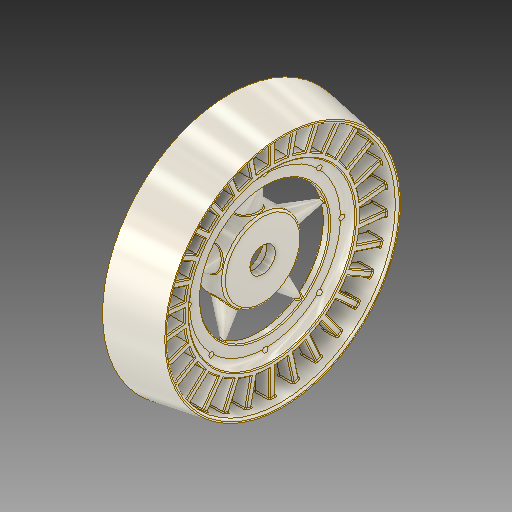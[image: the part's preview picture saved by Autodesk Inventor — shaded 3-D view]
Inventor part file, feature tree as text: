
AUTODESK INVENTOR PART (.ipt)
format: ipt  version: 2019 (Build 230136000, 136)  size: 1,782,272 bytes
history: native  units: mm
features: sketch x12, extrude x8, other x4, pattern_circular x3, fillet x2, plane x2, split x2, surface_op x2, revolve x1, loft x1, boolean_combine x1
ambient origin geometry x8: Origin, YZ Plane, XZ Plane, XY Plane, X Axis, Y Axis, Z Axis, Center Point
bodies: Solid2 (feature_tree), Solid1 (feature_tree)
feature tree (38):
  extrude  "Extrusion1"  Depth=180.0mm
  revolve  "Revolution1"  [1 undecoded]
  extrude  "Extrusion2"  Depth=2.0mm
  fillet  "Fillet1"  Radius=25.394541mm
  extrude  "Extrusion3"  TaperAngle=90.0deg  [1 undecoded]
  pattern_circular  "Circular Pattern1"  Count=17  [1 undecoded]
  other  "Rule Fillet1"
  plane  "Work Plane1"
  extrude  "Extrusion4"  Depth=8.0mm
  extrude  "Extrusion5"  Depth=30.0mm
  extrude  "Extrusion6"  Depth=300.0mm TaperAngle=360.0deg
  extrude  "Extrusion7"  Depth=25.0mm
  fillet  "Fillet2"  Radius=80.0mm
  sketch  "Sketch9"  dims[d33=30.0mm d34=0.0mm d35=72.0mm]
  sketch  "Sketch10"  dims[d36=5.18mm d37=0.0mm]
  plane  "Work Plane2"
  loft  "Loft1"
  split  "Split1"
  split  "Split2"
  pattern_circular  "Circular Pattern2"  [2 undecoded]
  boolean_combine  "Combine1"
  other  "Rule Fillet2"
  extrude  "Extrusion8"  Depth=10.0mm TaperAngle=0.0deg
  pattern_circular  "Circular Pattern3"  [2 undecoded]
  sketch  "Sketch1"  dims[d2=132.0mm d3=180.0mm]
  sketch  "Sketch2"  dims[d4=15.0mm d5=0.0mm d8=4.363323mm]
  sketch  "Sketch3"  dims[d10=54.5mm d15=2.0mm d16=25.394541mm]
  sketch  "Sketch4"  dims[d17=12.5mm d18=90.0deg d19=170.0mm]
  sketch  "Sketch5"  dims[d20=7.5mm d21=0.0mm d22=8.0mm]
  sketch  "Sketch6"  dims[d23=6.0mm d24=30.0mm]
  sketch  "Sketch7"  dims[d25=7.687mm d26=0.0mm d27=300.0mm d28=360.0deg]
  sketch  "Sketch8"  dims[d30=1.0mm d31=25.0mm d32=80.0mm]
  sketch  "Sketch11"  dims[d38=56.0mm]
  sketch  "Sketch12"  dims[d39=16.0mm d40=0.0mm d41=26.0mm d42=16.0mm d43=0.0mm d44=2.0mm d45=50.0mm d46=30.0mm d47=1.0mm d48=5.0mm d49=70.0mm d50=0.0mm d51=90.0deg d52=0.0mm d53=90.0deg d54=50.0mm d55=360.0deg d57=1.0mm d58=156.0mm d59=5.2mm d60=10.0mm d61=0.0mm d62=80.0mm d63=360.0deg d65=117.0mm d66=25.5mm]
  surface_op  "Surface1"
  surface_op  "Surface2"
  other  "Srf1"
  other  "Srf2"
note: 7 required parameter values undecoded (feature->parameter linkage not recoverable at this tier; creation-order binding heuristic only, values carry confidence <= 0.55)